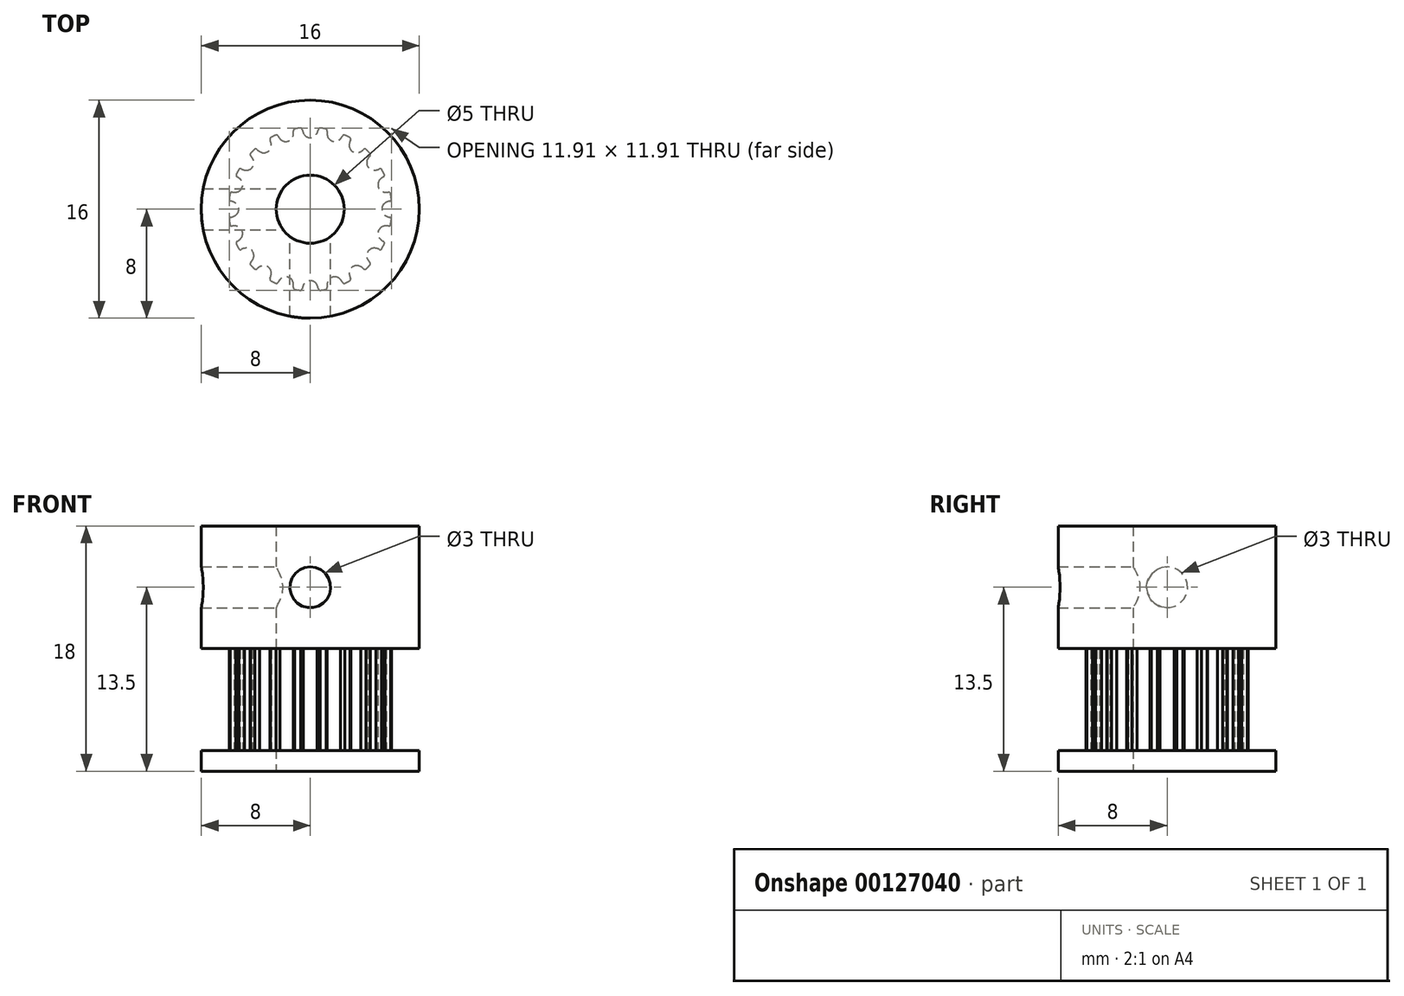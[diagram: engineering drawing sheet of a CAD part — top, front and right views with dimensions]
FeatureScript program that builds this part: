
annotation { "Feature Type Name" : "Feature", "Feature Type Description" : "" }
export const myFeature = defineFeature(function(context is Context, id is Id, definition is map)
    precondition{}
    {
        {
            var Q0;
            Q0=qCreatedBy(makeId("Top.planeOp"),FACE);
            var sketch = newSketch(context, id + "F0", { "sketchPlane" : qUnion([Q0])});
            skLineSegment(sketch, "E0", {"start": v(-19.17, 17.78) * mm, "end": v(-18.17, 17.78) * mm});
            skLineSegment(sketch, "E1", {"start": v(-18.17, 17.78) * mm, "end": v(-18.17, 18.4) * mm});
            skArc(sketch, "E2", {"start": v(-18.67, 18.85) * mm, "mid": v(-18.88, 19.07) * mm, "end": v(-19.17, 19.16) * mm});
            skArc(sketch, "E3", {"start": v(-18.58, 18.54) * mm, "mid": v(-18.61, 18.7) * mm, "end": v(-18.67, 18.85) * mm});
            skArc(sketch, "E4", {"start": v(-18.58, 18.54) * mm, "mid": v(-18.53, 18.44) * mm, "end": v(-18.43, 18.4) * mm});
            skLineSegment(sketch, "E5", {"start": v(-18.43, 18.4) * mm, "end": v(-18.17, 18.4) * mm});
            skArc(sketch, "E6.0.MirrorCS", {"start": v(-19.67, 18.85) * mm, "mid": v(-19.47, 19.07) * mm, "end": v(-19.17, 19.16) * mm});
            skArc(sketch, "E7.0.MirrorCS", {"start": v(-19.76, 18.54) * mm, "mid": v(-19.73, 18.7) * mm, "end": v(-19.67, 18.85) * mm});
            skArc(sketch, "E8.0.MirrorCS", {"start": v(-19.76, 18.54) * mm, "mid": v(-19.81, 18.44) * mm, "end": v(-19.91, 18.4) * mm});
            skLineSegment(sketch, "E9.0.MirrorCS", {"start": v(-19.91, 18.4) * mm, "end": v(-20.17, 18.4) * mm});
            skLineSegment(sketch, "E10.0.MirrorCS", {"start": v(-20.17, 17.78) * mm, "end": v(-20.17, 18.4) * mm});
            skLineSegment(sketch, "E11.0.MirrorCS", {"start": v(-19.17, 17.78) * mm, "end": v(-20.17, 17.78) * mm});
            skLineSegment(sketch, "E12.direction1", {"start": v(-20.17, 17.78) * mm, "end": v(-18.17, 17.78) * mm, "construction": true});
            skLineSegment(sketch, "E13", {"start": v(-20.17, 18.15) * mm, "end": v(-18.17, 18.15) * mm, "construction": true});
            skPoint(sketch, "E14", {"position": v(0, -5.25) * mm});
            skArc(sketch, "E15", {"start": v(0.51, -5.6) * mm, "mid": v(0, -5.25) * mm, "end": v(-0.51, -5.6) * mm});
            skArc(sketch, "E16", {"start": v(-0.51, -5.6) * mm, "mid": v(-0.56, -5.71) * mm, "end": v(-0.59, -5.83) * mm});
            skArc(sketch, "E17", {"start": v(0.59, -5.83) * mm, "mid": v(0.56, -5.71) * mm, "end": v(0.51, -5.6) * mm});
            skArc(sketch, "E18", {"start": v(0.72, -5.96) * mm, "mid": v(0.94, -5.93) * mm, "end": v(1.16, -5.89) * mm});
            skArc(sketch, "E19", {"start": v(0.59, -5.83) * mm, "mid": v(0.66, -5.94) * mm, "end": v(0.8, -5.95) * mm});
            skArc(sketch, "E20", {"start": v(-0.59, -5.83) * mm, "mid": v(-0.66, -5.94) * mm, "end": v(-0.8, -5.95) * mm});
            skArc(sketch, "E21.1.0", {"start": v(2.22, -5.16) * mm, "mid": v(1.62, -5) * mm, "end": v(1.24, -5.48) * mm});
            skPoint(sketch, "E21.1.1", {"position": v(1.62, -5) * mm});
            skArc(sketch, "E21.1.2", {"start": v(1.24, -5.48) * mm, "mid": v(1.23, -5.6) * mm, "end": v(1.24, -5.73) * mm});
            skArc(sketch, "E21.1.3", {"start": v(2.36, -5.37) * mm, "mid": v(2.47, -5.44) * mm, "end": v(2.6, -5.41) * mm});
            skArc(sketch, "E21.1.4", {"start": v(1.24, -5.73) * mm, "mid": v(1.2, -5.85) * mm, "end": v(1.08, -5.9) * mm});
            skArc(sketch, "E21.1.5", {"start": v(2.36, -5.37) * mm, "mid": v(2.3, -5.26) * mm, "end": v(2.22, -5.16) * mm});
            skArc(sketch, "E22.3.2.0", {"start": v(3.7, -4.22) * mm, "mid": v(3.09, -4.25) * mm, "end": v(2.87, -4.83) * mm});
            skPoint(sketch, "E22.4.2.0", {"position": v(3.09, -4.25) * mm});
            skArc(sketch, "E22.5.2.0", {"start": v(2.87, -4.83) * mm, "mid": v(2.9, -4.95) * mm, "end": v(2.95, -5.07) * mm});
            skArc(sketch, "E22.9.2.0", {"start": v(3.9, -4.37) * mm, "mid": v(4.03, -4.41) * mm, "end": v(4.14, -4.35) * mm});
            skArc(sketch, "E22.13.2.0", {"start": v(2.95, -5.07) * mm, "mid": v(2.95, -5.2) * mm, "end": v(2.85, -5.28) * mm});
            skArc(sketch, "E22.17.2.0", {"start": v(3.9, -4.37) * mm, "mid": v(3.81, -4.3) * mm, "end": v(3.7, -4.22) * mm});
            skArc(sketch, "E22.3.3.0", {"start": v(4.83, -2.87) * mm, "mid": v(4.25, -3.09) * mm, "end": v(4.22, -3.7) * mm});
            skPoint(sketch, "E22.4.3.0", {"position": v(4.25, -3.09) * mm});
            skArc(sketch, "E22.5.3.0", {"start": v(4.22, -3.7) * mm, "mid": v(4.3, -3.81) * mm, "end": v(4.37, -3.9) * mm});
            skArc(sketch, "E22.9.3.0", {"start": v(5.07, -2.95) * mm, "mid": v(5.2, -2.95) * mm, "end": v(5.28, -2.85) * mm});
            skArc(sketch, "E22.13.3.0", {"start": v(4.37, -3.9) * mm, "mid": v(4.41, -4.03) * mm, "end": v(4.35, -4.14) * mm});
            skArc(sketch, "E22.17.3.0", {"start": v(5.07, -2.95) * mm, "mid": v(4.95, -2.9) * mm, "end": v(4.83, -2.87) * mm});
            skArc(sketch, "E22.3.4.0", {"start": v(5.48, -1.24) * mm, "mid": v(5, -1.62) * mm, "end": v(5.16, -2.22) * mm});
            skPoint(sketch, "E22.4.4.0", {"position": v(5, -1.62) * mm});
            skArc(sketch, "E22.5.4.0", {"start": v(5.16, -2.22) * mm, "mid": v(5.26, -2.3) * mm, "end": v(5.37, -2.36) * mm});
            skArc(sketch, "E22.9.4.0", {"start": v(5.73, -1.24) * mm, "mid": v(5.85, -1.2) * mm, "end": v(5.9, -1.08) * mm});
            skArc(sketch, "E22.13.4.0", {"start": v(5.37, -2.36) * mm, "mid": v(5.44, -2.47) * mm, "end": v(5.41, -2.6) * mm});
            skArc(sketch, "E22.17.4.0", {"start": v(5.73, -1.24) * mm, "mid": v(5.6, -1.23) * mm, "end": v(5.48, -1.24) * mm});
            skArc(sketch, "E22.3.5.0", {"start": v(5.6, 0.51) * mm, "mid": v(5.25, 0) * mm, "end": v(5.6, -0.51) * mm});
            skPoint(sketch, "E22.4.5.0", {"position": v(5.25, 0) * mm});
            skArc(sketch, "E22.5.5.0", {"start": v(5.6, -0.51) * mm, "mid": v(5.71, -0.56) * mm, "end": v(5.83, -0.59) * mm});
            skArc(sketch, "E22.9.5.0", {"start": v(5.83, 0.59) * mm, "mid": v(5.94, 0.66) * mm, "end": v(5.95, 0.8) * mm});
            skArc(sketch, "E22.13.5.0", {"start": v(5.83, -0.59) * mm, "mid": v(5.94, -0.66) * mm, "end": v(5.95, -0.8) * mm});
            skArc(sketch, "E22.17.5.0", {"start": v(5.83, 0.59) * mm, "mid": v(5.71, 0.56) * mm, "end": v(5.6, 0.51) * mm});
            skArc(sketch, "E22.3.6.0", {"start": v(5.16, 2.22) * mm, "mid": v(5, 1.62) * mm, "end": v(5.48, 1.24) * mm});
            skPoint(sketch, "E22.4.6.0", {"position": v(5, 1.62) * mm});
            skArc(sketch, "E22.5.6.0", {"start": v(5.48, 1.24) * mm, "mid": v(5.6, 1.23) * mm, "end": v(5.73, 1.24) * mm});
            skArc(sketch, "E22.9.6.0", {"start": v(5.37, 2.36) * mm, "mid": v(5.44, 2.47) * mm, "end": v(5.41, 2.6) * mm});
            skArc(sketch, "E22.13.6.0", {"start": v(5.73, 1.24) * mm, "mid": v(5.85, 1.2) * mm, "end": v(5.9, 1.08) * mm});
            skArc(sketch, "E22.17.6.0", {"start": v(5.37, 2.36) * mm, "mid": v(5.26, 2.3) * mm, "end": v(5.16, 2.22) * mm});
            skArc(sketch, "E22.3.7.0", {"start": v(4.22, 3.7) * mm, "mid": v(4.25, 3.09) * mm, "end": v(4.83, 2.87) * mm});
            skPoint(sketch, "E22.4.7.0", {"position": v(4.25, 3.09) * mm});
            skArc(sketch, "E22.5.7.0", {"start": v(4.83, 2.87) * mm, "mid": v(4.95, 2.9) * mm, "end": v(5.07, 2.95) * mm});
            skArc(sketch, "E22.9.7.0", {"start": v(4.37, 3.9) * mm, "mid": v(4.41, 4.03) * mm, "end": v(4.35, 4.14) * mm});
            skArc(sketch, "E22.13.7.0", {"start": v(5.07, 2.95) * mm, "mid": v(5.2, 2.95) * mm, "end": v(5.28, 2.85) * mm});
            skArc(sketch, "E22.17.7.0", {"start": v(4.37, 3.9) * mm, "mid": v(4.3, 3.81) * mm, "end": v(4.22, 3.7) * mm});
            skArc(sketch, "E22.3.8.0", {"start": v(2.87, 4.83) * mm, "mid": v(3.09, 4.25) * mm, "end": v(3.7, 4.22) * mm});
            skPoint(sketch, "E22.4.8.0", {"position": v(3.09, 4.25) * mm});
            skArc(sketch, "E22.5.8.0", {"start": v(3.7, 4.22) * mm, "mid": v(3.81, 4.3) * mm, "end": v(3.9, 4.37) * mm});
            skArc(sketch, "E22.9.8.0", {"start": v(2.95, 5.07) * mm, "mid": v(2.95, 5.2) * mm, "end": v(2.85, 5.28) * mm});
            skArc(sketch, "E22.13.8.0", {"start": v(3.9, 4.37) * mm, "mid": v(4.03, 4.41) * mm, "end": v(4.14, 4.35) * mm});
            skArc(sketch, "E22.17.8.0", {"start": v(2.95, 5.07) * mm, "mid": v(2.9, 4.95) * mm, "end": v(2.87, 4.83) * mm});
            skArc(sketch, "E22.3.9.0", {"start": v(1.24, 5.48) * mm, "mid": v(1.62, 5) * mm, "end": v(2.22, 5.16) * mm});
            skPoint(sketch, "E22.4.9.0", {"position": v(1.62, 5) * mm});
            skArc(sketch, "E22.5.9.0", {"start": v(2.22, 5.16) * mm, "mid": v(2.3, 5.26) * mm, "end": v(2.36, 5.37) * mm});
            skArc(sketch, "E22.9.9.0", {"start": v(1.24, 5.73) * mm, "mid": v(1.2, 5.85) * mm, "end": v(1.08, 5.9) * mm});
            skArc(sketch, "E22.13.9.0", {"start": v(2.36, 5.37) * mm, "mid": v(2.47, 5.44) * mm, "end": v(2.6, 5.41) * mm});
            skArc(sketch, "E22.17.9.0", {"start": v(1.24, 5.73) * mm, "mid": v(1.23, 5.6) * mm, "end": v(1.24, 5.48) * mm});
            skArc(sketch, "E22.3.10.0", {"start": v(-0.51, 5.6) * mm, "mid": v(0, 5.25) * mm, "end": v(0.51, 5.6) * mm});
            skPoint(sketch, "E22.4.10.0", {"position": v(0, 5.25) * mm});
            skArc(sketch, "E22.5.10.0", {"start": v(0.51, 5.6) * mm, "mid": v(0.56, 5.71) * mm, "end": v(0.59, 5.83) * mm});
            skArc(sketch, "E22.9.10.0", {"start": v(-0.59, 5.83) * mm, "mid": v(-0.66, 5.94) * mm, "end": v(-0.8, 5.95) * mm});
            skArc(sketch, "E22.13.10.0", {"start": v(0.59, 5.83) * mm, "mid": v(0.66, 5.94) * mm, "end": v(0.8, 5.95) * mm});
            skArc(sketch, "E22.17.10.0", {"start": v(-0.59, 5.83) * mm, "mid": v(-0.56, 5.71) * mm, "end": v(-0.51, 5.6) * mm});
            skArc(sketch, "E22.3.11.0", {"start": v(-2.22, 5.16) * mm, "mid": v(-1.62, 5) * mm, "end": v(-1.24, 5.48) * mm});
            skPoint(sketch, "E22.4.11.0", {"position": v(-1.62, 5) * mm});
            skArc(sketch, "E22.5.11.0", {"start": v(-1.24, 5.48) * mm, "mid": v(-1.23, 5.6) * mm, "end": v(-1.24, 5.73) * mm});
            skArc(sketch, "E22.9.11.0", {"start": v(-2.36, 5.37) * mm, "mid": v(-2.47, 5.44) * mm, "end": v(-2.6, 5.41) * mm});
            skArc(sketch, "E22.13.11.0", {"start": v(-1.24, 5.73) * mm, "mid": v(-1.2, 5.85) * mm, "end": v(-1.08, 5.9) * mm});
            skArc(sketch, "E22.17.11.0", {"start": v(-2.36, 5.37) * mm, "mid": v(-2.3, 5.26) * mm, "end": v(-2.22, 5.16) * mm});
            skArc(sketch, "E22.3.12.0", {"start": v(-3.7, 4.22) * mm, "mid": v(-3.09, 4.25) * mm, "end": v(-2.87, 4.83) * mm});
            skPoint(sketch, "E22.4.12.0", {"position": v(-3.09, 4.25) * mm});
            skArc(sketch, "E22.5.12.0", {"start": v(-2.87, 4.83) * mm, "mid": v(-2.9, 4.95) * mm, "end": v(-2.95, 5.07) * mm});
            skArc(sketch, "E22.9.12.0", {"start": v(-3.9, 4.37) * mm, "mid": v(-4.03, 4.41) * mm, "end": v(-4.14, 4.35) * mm});
            skArc(sketch, "E22.13.12.0", {"start": v(-2.95, 5.07) * mm, "mid": v(-2.95, 5.2) * mm, "end": v(-2.85, 5.28) * mm});
            skArc(sketch, "E22.17.12.0", {"start": v(-3.9, 4.37) * mm, "mid": v(-3.81, 4.3) * mm, "end": v(-3.7, 4.22) * mm});
            skArc(sketch, "E22.3.13.0", {"start": v(-4.83, 2.87) * mm, "mid": v(-4.25, 3.09) * mm, "end": v(-4.22, 3.7) * mm});
            skPoint(sketch, "E22.4.13.0", {"position": v(-4.25, 3.09) * mm});
            skArc(sketch, "E22.5.13.0", {"start": v(-4.22, 3.7) * mm, "mid": v(-4.3, 3.81) * mm, "end": v(-4.37, 3.9) * mm});
            skArc(sketch, "E22.9.13.0", {"start": v(-5.07, 2.95) * mm, "mid": v(-5.2, 2.95) * mm, "end": v(-5.28, 2.85) * mm});
            skArc(sketch, "E22.13.13.0", {"start": v(-4.37, 3.9) * mm, "mid": v(-4.41, 4.03) * mm, "end": v(-4.35, 4.14) * mm});
            skArc(sketch, "E22.17.13.0", {"start": v(-5.07, 2.95) * mm, "mid": v(-4.95, 2.9) * mm, "end": v(-4.83, 2.87) * mm});
            skArc(sketch, "E22.3.14.0", {"start": v(-5.48, 1.24) * mm, "mid": v(-5, 1.62) * mm, "end": v(-5.16, 2.22) * mm});
            skPoint(sketch, "E22.4.14.0", {"position": v(-5, 1.62) * mm});
            skArc(sketch, "E22.5.14.0", {"start": v(-5.16, 2.22) * mm, "mid": v(-5.26, 2.3) * mm, "end": v(-5.37, 2.36) * mm});
            skArc(sketch, "E22.9.14.0", {"start": v(-5.73, 1.24) * mm, "mid": v(-5.85, 1.2) * mm, "end": v(-5.9, 1.08) * mm});
            skArc(sketch, "E22.13.14.0", {"start": v(-5.37, 2.36) * mm, "mid": v(-5.44, 2.47) * mm, "end": v(-5.41, 2.6) * mm});
            skArc(sketch, "E22.17.14.0", {"start": v(-5.73, 1.24) * mm, "mid": v(-5.6, 1.23) * mm, "end": v(-5.48, 1.24) * mm});
            skArc(sketch, "E22.3.15.0", {"start": v(-5.6, -0.51) * mm, "mid": v(-5.25, 0) * mm, "end": v(-5.6, 0.51) * mm});
            skPoint(sketch, "E22.4.15.0", {"position": v(-5.25, 0) * mm});
            skArc(sketch, "E22.5.15.0", {"start": v(-5.6, 0.51) * mm, "mid": v(-5.71, 0.56) * mm, "end": v(-5.83, 0.59) * mm});
            skArc(sketch, "E22.9.15.0", {"start": v(-5.83, -0.59) * mm, "mid": v(-5.94, -0.66) * mm, "end": v(-5.95, -0.8) * mm});
            skArc(sketch, "E22.13.15.0", {"start": v(-5.83, 0.59) * mm, "mid": v(-5.94, 0.66) * mm, "end": v(-5.95, 0.8) * mm});
            skArc(sketch, "E22.17.15.0", {"start": v(-5.83, -0.59) * mm, "mid": v(-5.71, -0.56) * mm, "end": v(-5.6, -0.51) * mm});
            skArc(sketch, "E22.3.16.0", {"start": v(-5.16, -2.22) * mm, "mid": v(-5, -1.62) * mm, "end": v(-5.48, -1.24) * mm});
            skPoint(sketch, "E22.4.16.0", {"position": v(-5, -1.62) * mm});
            skArc(sketch, "E22.5.16.0", {"start": v(-5.48, -1.24) * mm, "mid": v(-5.6, -1.23) * mm, "end": v(-5.73, -1.24) * mm});
            skArc(sketch, "E22.9.16.0", {"start": v(-5.37, -2.36) * mm, "mid": v(-5.44, -2.47) * mm, "end": v(-5.41, -2.6) * mm});
            skArc(sketch, "E22.13.16.0", {"start": v(-5.73, -1.24) * mm, "mid": v(-5.85, -1.2) * mm, "end": v(-5.9, -1.08) * mm});
            skArc(sketch, "E22.17.16.0", {"start": v(-5.37, -2.36) * mm, "mid": v(-5.26, -2.3) * mm, "end": v(-5.16, -2.22) * mm});
            skArc(sketch, "E22.3.17.0", {"start": v(-4.22, -3.7) * mm, "mid": v(-4.25, -3.09) * mm, "end": v(-4.83, -2.87) * mm});
            skPoint(sketch, "E22.4.17.0", {"position": v(-4.25, -3.09) * mm});
            skArc(sketch, "E22.5.17.0", {"start": v(-4.83, -2.87) * mm, "mid": v(-4.95, -2.9) * mm, "end": v(-5.07, -2.95) * mm});
            skArc(sketch, "E22.9.17.0", {"start": v(-4.37, -3.9) * mm, "mid": v(-4.41, -4.03) * mm, "end": v(-4.35, -4.14) * mm});
            skArc(sketch, "E22.13.17.0", {"start": v(-5.07, -2.95) * mm, "mid": v(-5.2, -2.95) * mm, "end": v(-5.28, -2.85) * mm});
            skArc(sketch, "E22.17.17.0", {"start": v(-4.37, -3.9) * mm, "mid": v(-4.3, -3.81) * mm, "end": v(-4.22, -3.7) * mm});
            skArc(sketch, "E22.3.18.0", {"start": v(-2.87, -4.83) * mm, "mid": v(-3.09, -4.25) * mm, "end": v(-3.7, -4.22) * mm});
            skPoint(sketch, "E22.4.18.0", {"position": v(-3.09, -4.25) * mm});
            skArc(sketch, "E22.5.18.0", {"start": v(-3.7, -4.22) * mm, "mid": v(-3.81, -4.3) * mm, "end": v(-3.9, -4.37) * mm});
            skArc(sketch, "E22.9.18.0", {"start": v(-2.95, -5.07) * mm, "mid": v(-2.95, -5.2) * mm, "end": v(-2.85, -5.28) * mm});
            skArc(sketch, "E22.13.18.0", {"start": v(-3.9, -4.37) * mm, "mid": v(-4.03, -4.41) * mm, "end": v(-4.14, -4.35) * mm});
            skArc(sketch, "E22.17.18.0", {"start": v(-2.95, -5.07) * mm, "mid": v(-2.9, -4.95) * mm, "end": v(-2.87, -4.83) * mm});
            skArc(sketch, "E22.3.19.0", {"start": v(-1.24, -5.48) * mm, "mid": v(-1.62, -5) * mm, "end": v(-2.22, -5.16) * mm});
            skPoint(sketch, "E22.4.19.0", {"position": v(-1.62, -5) * mm});
            skArc(sketch, "E22.5.19.0", {"start": v(-2.22, -5.16) * mm, "mid": v(-2.3, -5.26) * mm, "end": v(-2.36, -5.37) * mm});
            skArc(sketch, "E22.9.19.0", {"start": v(-1.24, -5.73) * mm, "mid": v(-1.2, -5.85) * mm, "end": v(-1.08, -5.9) * mm});
            skArc(sketch, "E22.13.19.0", {"start": v(-2.36, -5.37) * mm, "mid": v(-2.47, -5.44) * mm, "end": v(-2.6, -5.41) * mm});
            skArc(sketch, "E22.17.19.0", {"start": v(-1.24, -5.73) * mm, "mid": v(-1.23, -5.6) * mm, "end": v(-1.24, -5.48) * mm});
            skArc(sketch, "E23.trimOffspring", {"start": v(2.52, -5.44) * mm, "mid": v(2.72, -5.35) * mm, "end": v(2.92, -5.24) * mm});
            skArc(sketch, "E24.trimOffspring", {"start": v(4.08, -4.4) * mm, "mid": v(4.24, -4.24) * mm, "end": v(4.4, -4.08) * mm});
            skArc(sketch, "E25.trimOffspring", {"start": v(5.24, -2.92) * mm, "mid": v(5.33, -2.76) * mm, "end": v(5.41, -2.6) * mm});
            skArc(sketch, "E26.trimOffspring", {"start": v(5.89, -1.16) * mm, "mid": v(5.93, -0.94) * mm, "end": v(5.96, -0.72) * mm});
            skArc(sketch, "E27.trimOffspring", {"start": v(5.44, 2.52) * mm, "mid": v(5.35, 2.72) * mm, "end": v(5.24, 2.92) * mm});
            skArc(sketch, "E28.trimOffspring", {"start": v(4.4, 4.08) * mm, "mid": v(4.24, 4.24) * mm, "end": v(4.08, 4.4) * mm});
            skArc(sketch, "E29.trimOffspring", {"start": v(5.96, 0.72) * mm, "mid": v(5.93, 0.94) * mm, "end": v(5.89, 1.16) * mm});
            skArc(sketch, "E30.trimOffspring", {"start": v(2.92, 5.24) * mm, "mid": v(2.72, 5.35) * mm, "end": v(2.52, 5.44) * mm});
            skArc(sketch, "E31.trimOffspring", {"start": v(1.16, 5.89) * mm, "mid": v(0.94, 5.93) * mm, "end": v(0.72, 5.96) * mm});
            skArc(sketch, "E32.trimOffspring", {"start": v(-0.72, 5.96) * mm, "mid": v(-0.94, 5.93) * mm, "end": v(-1.16, 5.89) * mm});
            skArc(sketch, "E33.trimOffspring", {"start": v(-2.52, 5.44) * mm, "mid": v(-2.72, 5.35) * mm, "end": v(-2.92, 5.24) * mm});
            skArc(sketch, "E34.trimOffspring", {"start": v(-4.08, 4.4) * mm, "mid": v(-4.24, 4.24) * mm, "end": v(-4.4, 4.08) * mm});
            skArc(sketch, "E35.trimOffspring", {"start": v(-5.24, 2.92) * mm, "mid": v(-5.35, 2.72) * mm, "end": v(-5.44, 2.52) * mm});
            skArc(sketch, "E36.trimOffspring", {"start": v(-5.89, 1.16) * mm, "mid": v(-5.93, 0.94) * mm, "end": v(-5.96, 0.72) * mm});
            skArc(sketch, "E37.trimOffspring", {"start": v(-5.96, -0.72) * mm, "mid": v(-5.93, -0.94) * mm, "end": v(-5.89, -1.16) * mm});
            skArc(sketch, "E38.trimOffspring", {"start": v(-5.44, -2.52) * mm, "mid": v(-5.35, -2.72) * mm, "end": v(-5.24, -2.92) * mm});
            skArc(sketch, "E39.trimOffspring", {"start": v(-4.4, -4.08) * mm, "mid": v(-4.24, -4.24) * mm, "end": v(-4.08, -4.4) * mm});
            skArc(sketch, "E40.trimOffspring", {"start": v(-2.92, -5.24) * mm, "mid": v(-2.72, -5.35) * mm, "end": v(-2.52, -5.44) * mm});
            skArc(sketch, "E41.trimOffspring", {"start": v(-1.16, -5.89) * mm, "mid": v(-0.94, -5.93) * mm, "end": v(-0.72, -5.96) * mm});
            skSolve(sketch);
        }
        {
            var Q0;
            Q0=makeQuery(id+"F0.imprint","IMPRINT",FACE,{"disambiguationData":[TD([[makeQuery(id+"F0.imprint","IMPRINT",EDGE,{"derivedFrom":sQuery(id+"F0.wireOp",EDGE,"E15")}),-1.0]])]});
            extrude(context, id + "F1", {"entities" : qUnion([Q0]), "depth" : 7.5 * mm});
        }
        {
            var Q0;
            Q0=makeQuery(id+"F1.opExtrude","CAP_FACE",FACE,{"disambiguationData":[OSD([sQuery(id+"F0.wireOp",EDGE,"E15"),sQuery(id+"F0.wireOp",EDGE,"E16"),sQuery(id+"F0.wireOp",EDGE,"E17"),sQuery(id+"F0.wireOp",EDGE,"E18"),sQuery(id+"F0.wireOp",EDGE,"E19"),sQuery(id+"F0.wireOp",EDGE,"E20"),sQuery(id+"F0.wireOp",EDGE,"E21.1.0"),sQuery(id+"F0.wireOp",EDGE,"E21.1.2"),sQuery(id+"F0.wireOp",EDGE,"E21.1.3"),sQuery(id+"F0.wireOp",EDGE,"E21.1.4"),sQuery(id+"F0.wireOp",EDGE,"E21.1.5"),sQuery(id+"F0.wireOp",EDGE,"E22.3.2.0"),sQuery(id+"F0.wireOp",EDGE,"E22.5.2.0"),sQuery(id+"F0.wireOp",EDGE,"E22.9.2.0"),sQuery(id+"F0.wireOp",EDGE,"E22.13.2.0"),sQuery(id+"F0.wireOp",EDGE,"E22.17.2.0"),sQuery(id+"F0.wireOp",EDGE,"E22.3.3.0"),sQuery(id+"F0.wireOp",EDGE,"E22.5.3.0"),sQuery(id+"F0.wireOp",EDGE,"E22.9.3.0"),sQuery(id+"F0.wireOp",EDGE,"E22.13.3.0"),sQuery(id+"F0.wireOp",EDGE,"E22.17.3.0"),sQuery(id+"F0.wireOp",EDGE,"E22.3.4.0"),sQuery(id+"F0.wireOp",EDGE,"E22.5.4.0"),sQuery(id+"F0.wireOp",EDGE,"E22.9.4.0"),sQuery(id+"F0.wireOp",EDGE,"E22.13.4.0"),sQuery(id+"F0.wireOp",EDGE,"E22.17.4.0"),sQuery(id+"F0.wireOp",EDGE,"E22.3.5.0"),sQuery(id+"F0.wireOp",EDGE,"E22.5.5.0"),sQuery(id+"F0.wireOp",EDGE,"E22.9.5.0"),sQuery(id+"F0.wireOp",EDGE,"E22.13.5.0"),sQuery(id+"F0.wireOp",EDGE,"E22.17.5.0"),sQuery(id+"F0.wireOp",EDGE,"E22.3.6.0"),sQuery(id+"F0.wireOp",EDGE,"E22.5.6.0"),sQuery(id+"F0.wireOp",EDGE,"E22.9.6.0"),sQuery(id+"F0.wireOp",EDGE,"E22.13.6.0"),sQuery(id+"F0.wireOp",EDGE,"E22.17.6.0"),sQuery(id+"F0.wireOp",EDGE,"E22.3.7.0"),sQuery(id+"F0.wireOp",EDGE,"E22.5.7.0"),sQuery(id+"F0.wireOp",EDGE,"E22.9.7.0"),sQuery(id+"F0.wireOp",EDGE,"E22.13.7.0"),sQuery(id+"F0.wireOp",EDGE,"E22.17.7.0"),sQuery(id+"F0.wireOp",EDGE,"E22.3.8.0"),sQuery(id+"F0.wireOp",EDGE,"E22.5.8.0"),sQuery(id+"F0.wireOp",EDGE,"E22.9.8.0"),sQuery(id+"F0.wireOp",EDGE,"E22.13.8.0"),sQuery(id+"F0.wireOp",EDGE,"E22.17.8.0"),sQuery(id+"F0.wireOp",EDGE,"E22.3.9.0"),sQuery(id+"F0.wireOp",EDGE,"E22.5.9.0"),sQuery(id+"F0.wireOp",EDGE,"E22.9.9.0"),sQuery(id+"F0.wireOp",EDGE,"E22.13.9.0"),sQuery(id+"F0.wireOp",EDGE,"E22.17.9.0"),sQuery(id+"F0.wireOp",EDGE,"E22.3.10.0"),sQuery(id+"F0.wireOp",EDGE,"E22.5.10.0"),sQuery(id+"F0.wireOp",EDGE,"E22.9.10.0"),sQuery(id+"F0.wireOp",EDGE,"E22.13.10.0"),sQuery(id+"F0.wireOp",EDGE,"E22.17.10.0"),sQuery(id+"F0.wireOp",EDGE,"E22.3.11.0"),sQuery(id+"F0.wireOp",EDGE,"E22.5.11.0"),sQuery(id+"F0.wireOp",EDGE,"E22.9.11.0"),sQuery(id+"F0.wireOp",EDGE,"E22.13.11.0"),sQuery(id+"F0.wireOp",EDGE,"E22.17.11.0"),sQuery(id+"F0.wireOp",EDGE,"E22.3.12.0"),sQuery(id+"F0.wireOp",EDGE,"E22.5.12.0"),sQuery(id+"F0.wireOp",EDGE,"E22.9.12.0"),sQuery(id+"F0.wireOp",EDGE,"E22.13.12.0"),sQuery(id+"F0.wireOp",EDGE,"E22.17.12.0"),sQuery(id+"F0.wireOp",EDGE,"E22.3.13.0"),sQuery(id+"F0.wireOp",EDGE,"E22.5.13.0"),sQuery(id+"F0.wireOp",EDGE,"E22.9.13.0"),sQuery(id+"F0.wireOp",EDGE,"E22.13.13.0"),sQuery(id+"F0.wireOp",EDGE,"E22.17.13.0"),sQuery(id+"F0.wireOp",EDGE,"E22.3.14.0"),sQuery(id+"F0.wireOp",EDGE,"E22.5.14.0"),sQuery(id+"F0.wireOp",EDGE,"E22.9.14.0"),sQuery(id+"F0.wireOp",EDGE,"E22.13.14.0"),sQuery(id+"F0.wireOp",EDGE,"E22.17.14.0"),sQuery(id+"F0.wireOp",EDGE,"E22.3.15.0"),sQuery(id+"F0.wireOp",EDGE,"E22.5.15.0"),sQuery(id+"F0.wireOp",EDGE,"E22.9.15.0"),sQuery(id+"F0.wireOp",EDGE,"E22.13.15.0"),sQuery(id+"F0.wireOp",EDGE,"E22.17.15.0"),sQuery(id+"F0.wireOp",EDGE,"E22.3.16.0"),sQuery(id+"F0.wireOp",EDGE,"E22.5.16.0"),sQuery(id+"F0.wireOp",EDGE,"E22.9.16.0"),sQuery(id+"F0.wireOp",EDGE,"E22.13.16.0"),sQuery(id+"F0.wireOp",EDGE,"E22.17.16.0"),sQuery(id+"F0.wireOp",EDGE,"E22.3.17.0"),sQuery(id+"F0.wireOp",EDGE,"E22.5.17.0"),sQuery(id+"F0.wireOp",EDGE,"E22.9.17.0"),sQuery(id+"F0.wireOp",EDGE,"E22.13.17.0"),sQuery(id+"F0.wireOp",EDGE,"E22.17.17.0"),sQuery(id+"F0.wireOp",EDGE,"E22.3.18.0"),sQuery(id+"F0.wireOp",EDGE,"E22.5.18.0"),sQuery(id+"F0.wireOp",EDGE,"E22.9.18.0"),sQuery(id+"F0.wireOp",EDGE,"E22.13.18.0"),sQuery(id+"F0.wireOp",EDGE,"E22.17.18.0"),sQuery(id+"F0.wireOp",EDGE,"E22.3.19.0"),sQuery(id+"F0.wireOp",EDGE,"E22.5.19.0"),sQuery(id+"F0.wireOp",EDGE,"E22.9.19.0"),sQuery(id+"F0.wireOp",EDGE,"E22.13.19.0"),sQuery(id+"F0.wireOp",EDGE,"E22.17.19.0"),sQuery(id+"F0.wireOp",EDGE,"E23.trimOffspring"),sQuery(id+"F0.wireOp",EDGE,"E24.trimOffspring"),sQuery(id+"F0.wireOp",EDGE,"E25.trimOffspring"),sQuery(id+"F0.wireOp",EDGE,"E26.trimOffspring"),sQuery(id+"F0.wireOp",EDGE,"E27.trimOffspring"),sQuery(id+"F0.wireOp",EDGE,"E28.trimOffspring"),sQuery(id+"F0.wireOp",EDGE,"E29.trimOffspring"),sQuery(id+"F0.wireOp",EDGE,"E30.trimOffspring"),sQuery(id+"F0.wireOp",EDGE,"E31.trimOffspring"),sQuery(id+"F0.wireOp",EDGE,"E32.trimOffspring"),sQuery(id+"F0.wireOp",EDGE,"E33.trimOffspring"),sQuery(id+"F0.wireOp",EDGE,"E34.trimOffspring"),sQuery(id+"F0.wireOp",EDGE,"E35.trimOffspring"),sQuery(id+"F0.wireOp",EDGE,"E36.trimOffspring"),sQuery(id+"F0.wireOp",EDGE,"E37.trimOffspring"),sQuery(id+"F0.wireOp",EDGE,"E38.trimOffspring"),sQuery(id+"F0.wireOp",EDGE,"E39.trimOffspring"),sQuery(id+"F0.wireOp",EDGE,"E40.trimOffspring"),sQuery(id+"F0.wireOp",EDGE,"E41.trimOffspring")])],"isStart":false});
            var sketch = newSketch(context, id + "F2", { "sketchPlane" : qUnion([Q0])});
            skCircle(sketch, "E42", {"center": v(0, 0) * mm, "radius": 8 * mm});
            skSolve(sketch);
        }
        {
            var Q0;
            Q0=qSketchRegion(id+"F2",true);
            extrude(context, id + "F3", {"entities" : qUnion([Q0]), "operationType" : NewBodyOperationType.ADD, "depth" : 9 * mm});
        }
        {
            var Q0;
            Q0=makeQuery(id+"F1.opExtrude","CAP_FACE",FACE,{"disambiguationData":[OSD([sQuery(id+"F0.wireOp",EDGE,"E15"),sQuery(id+"F0.wireOp",EDGE,"E16"),sQuery(id+"F0.wireOp",EDGE,"E17"),sQuery(id+"F0.wireOp",EDGE,"E18"),sQuery(id+"F0.wireOp",EDGE,"E19"),sQuery(id+"F0.wireOp",EDGE,"E20"),sQuery(id+"F0.wireOp",EDGE,"E21.1.0"),sQuery(id+"F0.wireOp",EDGE,"E21.1.2"),sQuery(id+"F0.wireOp",EDGE,"E21.1.3"),sQuery(id+"F0.wireOp",EDGE,"E21.1.4"),sQuery(id+"F0.wireOp",EDGE,"E21.1.5"),sQuery(id+"F0.wireOp",EDGE,"E22.3.2.0"),sQuery(id+"F0.wireOp",EDGE,"E22.5.2.0"),sQuery(id+"F0.wireOp",EDGE,"E22.9.2.0"),sQuery(id+"F0.wireOp",EDGE,"E22.13.2.0"),sQuery(id+"F0.wireOp",EDGE,"E22.17.2.0"),sQuery(id+"F0.wireOp",EDGE,"E22.3.3.0"),sQuery(id+"F0.wireOp",EDGE,"E22.5.3.0"),sQuery(id+"F0.wireOp",EDGE,"E22.9.3.0"),sQuery(id+"F0.wireOp",EDGE,"E22.13.3.0"),sQuery(id+"F0.wireOp",EDGE,"E22.17.3.0"),sQuery(id+"F0.wireOp",EDGE,"E22.3.4.0"),sQuery(id+"F0.wireOp",EDGE,"E22.5.4.0"),sQuery(id+"F0.wireOp",EDGE,"E22.9.4.0"),sQuery(id+"F0.wireOp",EDGE,"E22.13.4.0"),sQuery(id+"F0.wireOp",EDGE,"E22.17.4.0"),sQuery(id+"F0.wireOp",EDGE,"E22.3.5.0"),sQuery(id+"F0.wireOp",EDGE,"E22.5.5.0"),sQuery(id+"F0.wireOp",EDGE,"E22.9.5.0"),sQuery(id+"F0.wireOp",EDGE,"E22.13.5.0"),sQuery(id+"F0.wireOp",EDGE,"E22.17.5.0"),sQuery(id+"F0.wireOp",EDGE,"E22.3.6.0"),sQuery(id+"F0.wireOp",EDGE,"E22.5.6.0"),sQuery(id+"F0.wireOp",EDGE,"E22.9.6.0"),sQuery(id+"F0.wireOp",EDGE,"E22.13.6.0"),sQuery(id+"F0.wireOp",EDGE,"E22.17.6.0"),sQuery(id+"F0.wireOp",EDGE,"E22.3.7.0"),sQuery(id+"F0.wireOp",EDGE,"E22.5.7.0"),sQuery(id+"F0.wireOp",EDGE,"E22.9.7.0"),sQuery(id+"F0.wireOp",EDGE,"E22.13.7.0"),sQuery(id+"F0.wireOp",EDGE,"E22.17.7.0"),sQuery(id+"F0.wireOp",EDGE,"E22.3.8.0"),sQuery(id+"F0.wireOp",EDGE,"E22.5.8.0"),sQuery(id+"F0.wireOp",EDGE,"E22.9.8.0"),sQuery(id+"F0.wireOp",EDGE,"E22.13.8.0"),sQuery(id+"F0.wireOp",EDGE,"E22.17.8.0"),sQuery(id+"F0.wireOp",EDGE,"E22.3.9.0"),sQuery(id+"F0.wireOp",EDGE,"E22.5.9.0"),sQuery(id+"F0.wireOp",EDGE,"E22.9.9.0"),sQuery(id+"F0.wireOp",EDGE,"E22.13.9.0"),sQuery(id+"F0.wireOp",EDGE,"E22.17.9.0"),sQuery(id+"F0.wireOp",EDGE,"E22.3.10.0"),sQuery(id+"F0.wireOp",EDGE,"E22.5.10.0"),sQuery(id+"F0.wireOp",EDGE,"E22.9.10.0"),sQuery(id+"F0.wireOp",EDGE,"E22.13.10.0"),sQuery(id+"F0.wireOp",EDGE,"E22.17.10.0"),sQuery(id+"F0.wireOp",EDGE,"E22.3.11.0"),sQuery(id+"F0.wireOp",EDGE,"E22.5.11.0"),sQuery(id+"F0.wireOp",EDGE,"E22.9.11.0"),sQuery(id+"F0.wireOp",EDGE,"E22.13.11.0"),sQuery(id+"F0.wireOp",EDGE,"E22.17.11.0"),sQuery(id+"F0.wireOp",EDGE,"E22.3.12.0"),sQuery(id+"F0.wireOp",EDGE,"E22.5.12.0"),sQuery(id+"F0.wireOp",EDGE,"E22.9.12.0"),sQuery(id+"F0.wireOp",EDGE,"E22.13.12.0"),sQuery(id+"F0.wireOp",EDGE,"E22.17.12.0"),sQuery(id+"F0.wireOp",EDGE,"E22.3.13.0"),sQuery(id+"F0.wireOp",EDGE,"E22.5.13.0"),sQuery(id+"F0.wireOp",EDGE,"E22.9.13.0"),sQuery(id+"F0.wireOp",EDGE,"E22.13.13.0"),sQuery(id+"F0.wireOp",EDGE,"E22.17.13.0"),sQuery(id+"F0.wireOp",EDGE,"E22.3.14.0"),sQuery(id+"F0.wireOp",EDGE,"E22.5.14.0"),sQuery(id+"F0.wireOp",EDGE,"E22.9.14.0"),sQuery(id+"F0.wireOp",EDGE,"E22.13.14.0"),sQuery(id+"F0.wireOp",EDGE,"E22.17.14.0"),sQuery(id+"F0.wireOp",EDGE,"E22.3.15.0"),sQuery(id+"F0.wireOp",EDGE,"E22.5.15.0"),sQuery(id+"F0.wireOp",EDGE,"E22.9.15.0"),sQuery(id+"F0.wireOp",EDGE,"E22.13.15.0"),sQuery(id+"F0.wireOp",EDGE,"E22.17.15.0"),sQuery(id+"F0.wireOp",EDGE,"E22.3.16.0"),sQuery(id+"F0.wireOp",EDGE,"E22.5.16.0"),sQuery(id+"F0.wireOp",EDGE,"E22.9.16.0"),sQuery(id+"F0.wireOp",EDGE,"E22.13.16.0"),sQuery(id+"F0.wireOp",EDGE,"E22.17.16.0"),sQuery(id+"F0.wireOp",EDGE,"E22.3.17.0"),sQuery(id+"F0.wireOp",EDGE,"E22.5.17.0"),sQuery(id+"F0.wireOp",EDGE,"E22.9.17.0"),sQuery(id+"F0.wireOp",EDGE,"E22.13.17.0"),sQuery(id+"F0.wireOp",EDGE,"E22.17.17.0"),sQuery(id+"F0.wireOp",EDGE,"E22.3.18.0"),sQuery(id+"F0.wireOp",EDGE,"E22.5.18.0"),sQuery(id+"F0.wireOp",EDGE,"E22.9.18.0"),sQuery(id+"F0.wireOp",EDGE,"E22.13.18.0"),sQuery(id+"F0.wireOp",EDGE,"E22.17.18.0"),sQuery(id+"F0.wireOp",EDGE,"E22.3.19.0"),sQuery(id+"F0.wireOp",EDGE,"E22.5.19.0"),sQuery(id+"F0.wireOp",EDGE,"E22.9.19.0"),sQuery(id+"F0.wireOp",EDGE,"E22.13.19.0"),sQuery(id+"F0.wireOp",EDGE,"E22.17.19.0"),sQuery(id+"F0.wireOp",EDGE,"E23.trimOffspring"),sQuery(id+"F0.wireOp",EDGE,"E24.trimOffspring"),sQuery(id+"F0.wireOp",EDGE,"E25.trimOffspring"),sQuery(id+"F0.wireOp",EDGE,"E26.trimOffspring"),sQuery(id+"F0.wireOp",EDGE,"E27.trimOffspring"),sQuery(id+"F0.wireOp",EDGE,"E28.trimOffspring"),sQuery(id+"F0.wireOp",EDGE,"E29.trimOffspring"),sQuery(id+"F0.wireOp",EDGE,"E30.trimOffspring"),sQuery(id+"F0.wireOp",EDGE,"E31.trimOffspring"),sQuery(id+"F0.wireOp",EDGE,"E32.trimOffspring"),sQuery(id+"F0.wireOp",EDGE,"E33.trimOffspring"),sQuery(id+"F0.wireOp",EDGE,"E34.trimOffspring"),sQuery(id+"F0.wireOp",EDGE,"E35.trimOffspring"),sQuery(id+"F0.wireOp",EDGE,"E36.trimOffspring"),sQuery(id+"F0.wireOp",EDGE,"E37.trimOffspring"),sQuery(id+"F0.wireOp",EDGE,"E38.trimOffspring"),sQuery(id+"F0.wireOp",EDGE,"E39.trimOffspring"),sQuery(id+"F0.wireOp",EDGE,"E40.trimOffspring"),sQuery(id+"F0.wireOp",EDGE,"E41.trimOffspring")])],"isStart":true});
            var sketch = newSketch(context, id + "F4", { "sketchPlane" : qUnion([Q0])});
            skCircle(sketch, "E43", {"center": v(0, 0) * mm, "radius": 8 * mm});
            skSolve(sketch);
        }
        {
            var Q0;
            Q0=qSketchRegion(id+"F4",true);
            extrude(context, id + "F5", {"entities" : qUnion([Q0]), "operationType" : NewBodyOperationType.ADD, "depth" : 1.5 * mm});
        }
        {
            var Q0;
            Q0=makeQuery(id+"F5.opExtrude","CAP_FACE",FACE,{"disambiguationData":[OSD([sQuery(id+"F4.wireOp",EDGE,"E43")])],"isStart":false});
            var sketch = newSketch(context, id + "F6", { "sketchPlane" : qUnion([Q0])});
            skCircle(sketch, "E44", {"center": v(0, 0) * mm, "radius": 2.5 * mm});
            skSolve(sketch);
        }
        {
            var Q0;
            Q0=qSketchRegion(id+"F6",true);
            extrude(context, id + "F7", {"entities" : qUnion([Q0]), "operationType" : NewBodyOperationType.REMOVE, "endBound" : BoundingType.THROUGH_ALL, "oppositeDirection" : true, "depth" : 25 * mm});
        }
        {
            var Q0;
            Q0=qCreatedBy(makeId("Right.planeOp"),FACE);
            var sketch = newSketch(context, id + "F8", { "sketchPlane" : qUnion([Q0])});
            skCircle(sketch, "E45", {"center": v(0, 12) * mm, "radius": 1.5 * mm});
            skSolve(sketch);
        }
        {
            var Q0;
            Q0=qSketchRegion(id+"F8",true);
            extrude(context, id + "F9", {"entities" : qUnion([Q0]), "operationType" : NewBodyOperationType.REMOVE, "endBound" : BoundingType.THROUGH_ALL, "oppositeDirection" : true, "depth" : 25 * mm});
        }
        {
            var Q0;
            Q0=qCreatedBy(makeId("Front.planeOp"),FACE);
            var sketch = newSketch(context, id + "F10", { "sketchPlane" : qUnion([Q0])});
            skCircle(sketch, "E46", {"center": v(0, 12) * mm, "radius": 1.5 * mm});
            skSolve(sketch);
        }
        {
            var Q0;
            Q0=makeQuery(id+"F10.imprint","IMPRINT",FACE,{"disambiguationData":[TD([[makeQuery(id+"F10.imprint","IMPRINT",EDGE,{"derivedFrom":sQuery(id+"F10.wireOp",EDGE,"E46")}),1.0]])]});
            extrude(context, id + "F11", {"entities" : qUnion([Q0]), "operationType" : NewBodyOperationType.REMOVE, "depth" : 10 * mm});
        }
    });
